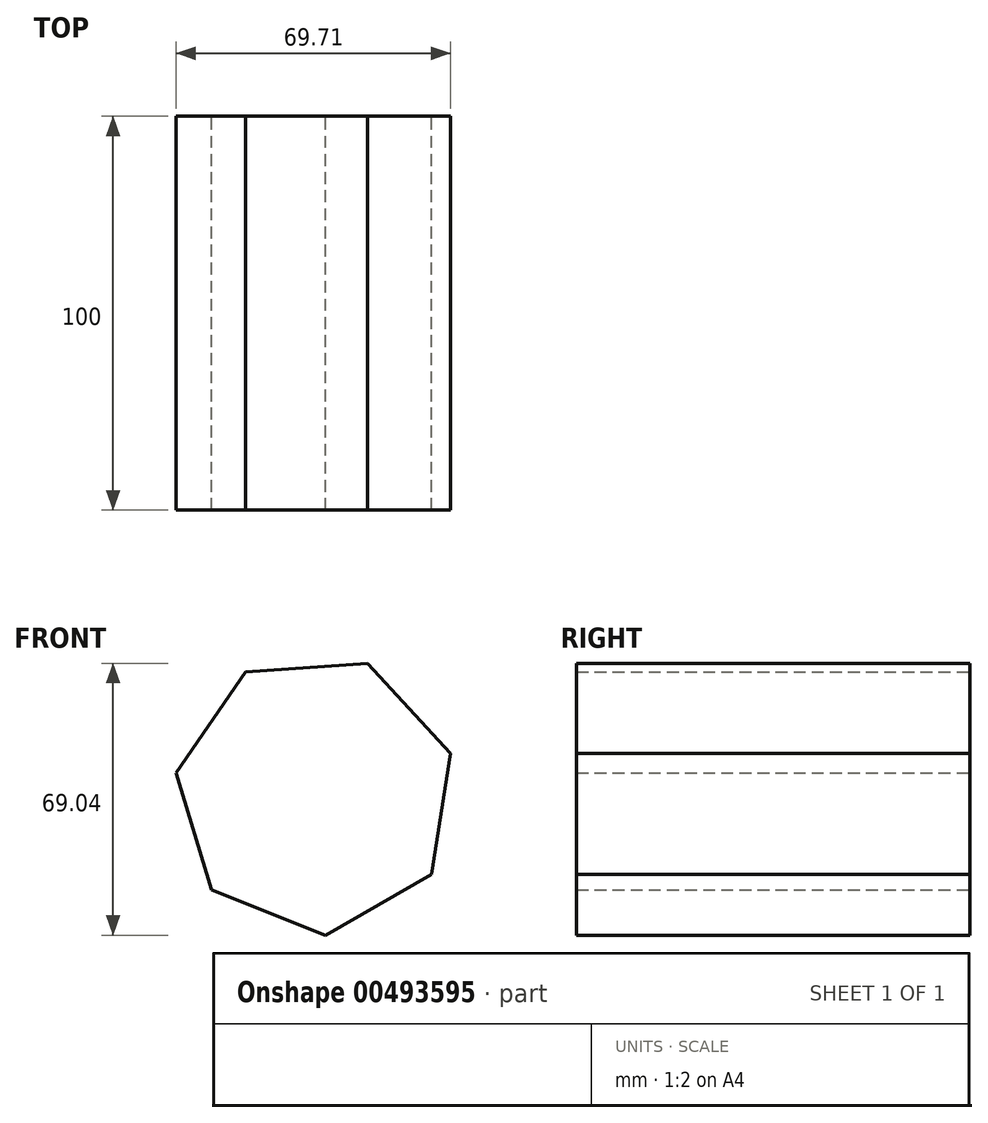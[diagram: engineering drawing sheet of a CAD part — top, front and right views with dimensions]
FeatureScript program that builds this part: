
annotation { "Feature Type Name" : "Feature", "Feature Type Description" : "" }
export const myFeature = defineFeature(function(context is Context, id is Id, definition is map)
    precondition{}
    {
        {
            var Q0;
            Q0=qCreatedBy(makeId("Front.planeOp"),FACE);
            var sketch = newSketch(context, id + "F0", { "sketchPlane" : qUnion([Q0])});
            skCircle(sketch, "E0.cCircle", {"center": v(0, 0) * mm, "radius": 35.84 * mm, "construction": true});
            skLineSegment(sketch, "E0.0", {"start": v(-26.4, -24.24) * mm, "end": v(-35.4, 5.52) * mm});
            skLineSegment(sketch, "E0.1", {"start": v(-35.4, 5.52) * mm, "end": v(-17.76, 31.13) * mm});
            skLineSegment(sketch, "E0.2", {"start": v(-17.76, 31.13) * mm, "end": v(13.26, 33.3) * mm});
            skLineSegment(sketch, "E0.3", {"start": v(13.26, 33.3) * mm, "end": v(34.3, 10.39) * mm});
            skLineSegment(sketch, "E0.4", {"start": v(34.3, 10.39) * mm, "end": v(29.5, -20.34) * mm});
            skLineSegment(sketch, "E0.5", {"start": v(29.5, -20.34) * mm, "end": v(2.5, -35.75) * mm});
            skLineSegment(sketch, "E0.6", {"start": v(2.5, -35.75) * mm, "end": v(-26.4, -24.24) * mm});
            skSolve(sketch);
        }
        {
            var Q0;
            Q0=makeQuery(id+"F0.imprint","IMPRINT",FACE,{"disambiguationData":[TD([[makeQuery(id+"F0.imprint","IMPRINT",EDGE,{"derivedFrom":sQuery(id+"F0.wireOp",EDGE,"E0.0")}),-1.0]])]});
            extrude(context, id + "F1", {"entities" : qUnion([Q0]), "endBound" : BoundingType.SYMMETRIC, "depth" : 100 * mm, "offsetDistance" : 25 * mm});
        }
    });
